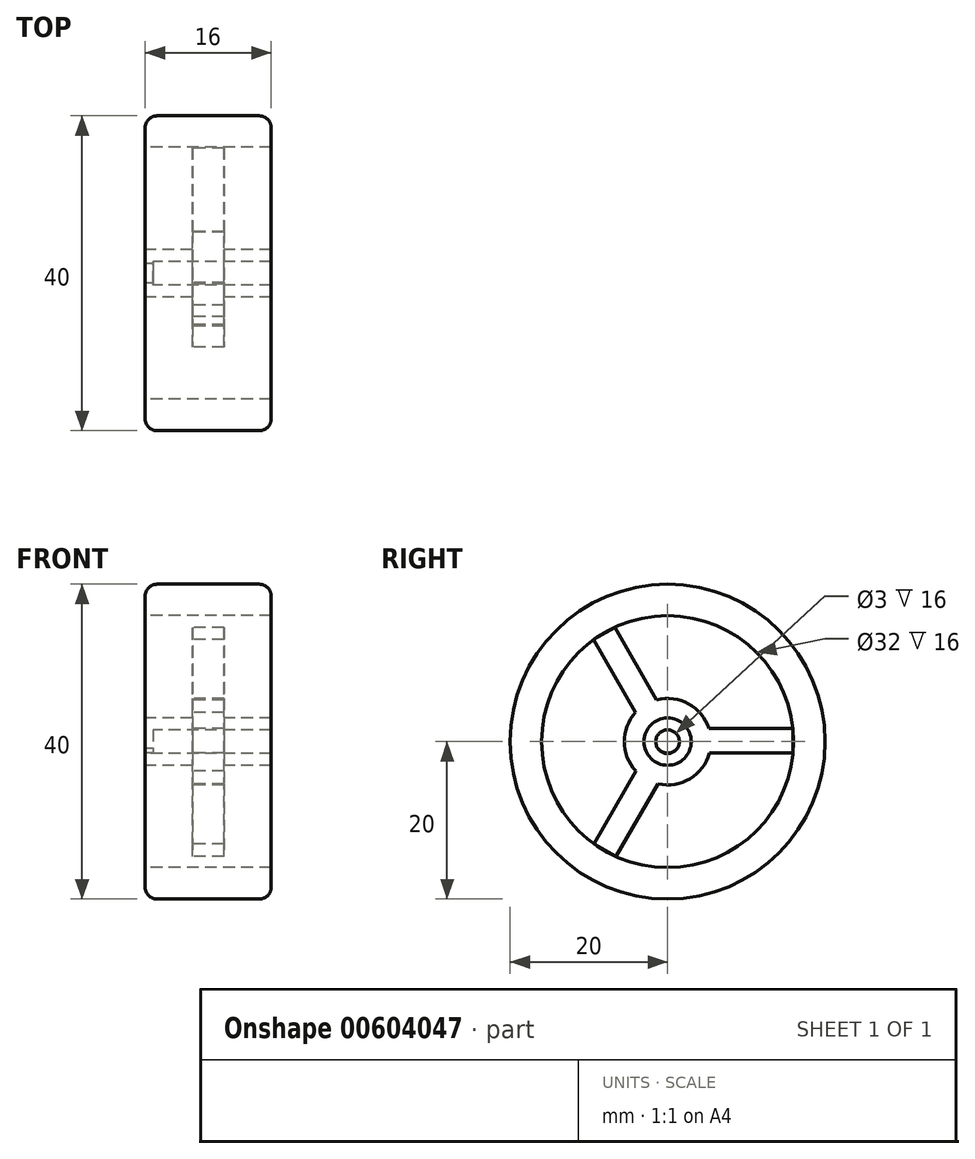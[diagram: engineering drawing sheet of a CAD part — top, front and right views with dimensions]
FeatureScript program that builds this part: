
annotation { "Feature Type Name" : "Feature", "Feature Type Description" : "" }
export const myFeature = defineFeature(function(context is Context, id is Id, definition is map)
    precondition{}
    {
        {
            var Q0;
            Q0=qCreatedBy(makeId("Front.planeOp"),FACE);
            var sketch = newSketch(context, id + "F0", { "sketchPlane" : qUnion([Q0])});
            skLineSegment(sketch, "E0.bottom", {"start": v(0, 0) * mm, "end": v(16, 0) * mm});
            skLineSegment(sketch, "E1.bottom", {"start": v(6, 0) * mm, "end": v(10, 0) * mm});
            skLineSegment(sketch, "E1.top", {"start": v(6, -16) * mm, "end": v(10, -16) * mm});
            skLineSegment(sketch, "E1.left", {"start": v(6, -13) * mm, "end": v(6, -14.5) * mm});
            skLineSegment(sketch, "E1.right", {"start": v(10, -13) * mm, "end": v(10, -14.5) * mm});
            skLineSegment(sketch, "E2.bottom", {"start": v(0, -16) * mm, "end": v(16, -16) * mm, "construction": true});
            skLineSegment(sketch, "E2.top", {"start": v(0, -13) * mm, "end": v(16, -13) * mm});
            skLineSegment(sketch, "E2.left", {"start": v(0, -14.5) * mm, "end": v(0, -13) * mm});
            skLineSegment(sketch, "E3", {"start": v(16, -14.5) * mm, "end": v(0, -14.5) * mm});
            skLineSegment(sketch, "E4", {"start": v(16, -14.5) * mm, "end": v(16, -13) * mm});
            skLineSegment(sketch, "E5.bottom", {"start": v(10, -13) * mm, "end": v(6, -13) * mm});
            skLineSegment(sketch, "E5.top", {"start": v(10, -10.5) * mm, "end": v(6, -10.5) * mm});
            skLineSegment(sketch, "E5.left", {"start": v(10, -13) * mm, "end": v(10, -10.5) * mm});
            skLineSegment(sketch, "E5.right", {"start": v(6, -13) * mm, "end": v(6, -10.5) * mm});
            skArc(sketch, "E6", {"start": v(1.5, 4) * mm, "mid": v(0.44, 3.56) * mm, "end": v(0, 2.5) * mm});
            skLineSegment(sketch, "E7", {"start": v(16, 4.74) * mm, "end": v(14.5, 4.74) * mm});
            skArc(sketch, "E8", {"start": v(16, 2.5) * mm, "mid": v(15.56, 3.56) * mm, "end": v(14.5, 4) * mm});
            skLineSegment(sketch, "E9", {"start": v(0, 2.5) * mm, "end": v(0, 0) * mm});
            skLineSegment(sketch, "E10", {"start": v(16, 0) * mm, "end": v(16, 2.5) * mm});
            skLineSegment(sketch, "E11", {"start": v(14.5, 4) * mm, "end": v(1.5, 4) * mm});
            skPoint(sketch, "E12.end.orphan", {"position": v(8, 0) * mm});
            skPoint(sketch, "E12.start.orphan", {"position": v(8, -10.5) * mm});
            skSolve(sketch);
        }
        {
            var Q0;
            Q0=qSketchRegion(id+"F0",true);
            var Q1;
            Q1=sQuery(id+"F0.wireOp",EDGE,"E1.top");
            revolve(context, id + "F1", {"entities" : qUnion([Q0]), "axis" : qUnion([Q1]), "revolveType" : RevolveType.FULL});
        }
        {
            var Q0;
            Q0=makeQuery(id+"F1.opRevolve","SWEPT_FACE",FACE,{"disambiguationData":[OSD([sQuery(id+"F0.wireOp",EDGE,"E5.right"),sQuery(id+"F0.wireOp",EDGE,"ZnnQBpbw-xC8R-MT8B-JQXv-VcrKk8POS6gG")])]});
            var sketch = newSketch(context, id + "F2", { "sketchPlane" : qUnion([Q0])});
            skLineSegment(sketch, "E13", {"start": v(-2.5, -14.35) * mm, "end": v(-15.91, -14.35) * mm});
            skLineSegment(sketch, "E14.1.1", {"start": v(-0.18, -19) * mm, "end": v(6.53, -30.6) * mm});
            skLineSegment(sketch, "E14.2.1", {"start": v(2.68, -14.65) * mm, "end": v(9.39, -3.04) * mm});
            skPoint(sketch, "E14.center", {"position": v(0, -16) * mm});
            skLineSegment(sketch, "E15", {"start": v(-15.91, -14.35) * mm, "end": v(-15.91, -17.46) * mm});
            skLineSegment(sketch, "E16", {"start": v(-15.91, -17.46) * mm, "end": v(-2.62, -17.46) * mm});
            skLineSegment(sketch, "E17", {"start": v(9.39, -3.04) * mm, "end": v(6.7, -1.49) * mm});
            skLineSegment(sketch, "E18", {"start": v(6.53, -30.6) * mm, "end": v(9.37, -28.97) * mm});
            skPoint(sketch, "E18.endSnap0", {"position": v(9.37, -29.3) * mm});
            skLineSegment(sketch, "E19", {"start": v(9.37, -28.97) * mm, "end": v(2.73, -17.46) * mm});
            skLineSegment(sketch, "E20", {"start": v(6.7, -1.49) * mm, "end": v(0.04, -13) * mm});
            skSolve(sketch);
        }
        {
            var Q0;
            {var subQ0=sQuery(id+"F2.wireOp",EDGE,"E17");Q0=makeQuery(id+"F2.imprint","IMPRINT",FACE,{"disambiguationData":[TD([[makeQuery(id+"F2.imprint","IMPRINT",EDGE,{"derivedFrom":subQ0}),1.0]])]});}
            var Q1;
            {var subQ0=sQuery(id+"F2.wireOp",EDGE,"E18");Q1=makeQuery(id+"F2.imprint","IMPRINT",FACE,{"disambiguationData":[TD([[makeQuery(id+"F2.imprint","IMPRINT",EDGE,{"derivedFrom":subQ0}),1.0]])]});}
            var Q2;
            {var subQ0=sQuery(id+"F2.wireOp",EDGE,"E15");Q2=makeQuery(id+"F2.imprint","IMPRINT",FACE,{"disambiguationData":[TD([[makeQuery(id+"F2.imprint","IMPRINT",EDGE,{"derivedFrom":subQ0}),1.0]])]});}
            extrude(context, id + "F3", {"entities" : qUnion([Q0, Q1, Q2]), "operationType" : NewBodyOperationType.ADD, "oppositeDirection" : true, "depth" : 4 * mm});
        }
        {
            var Q0;
            Q0=qCreatedBy(makeId("Right.planeOp"),FACE);
            var sketch = newSketch(context, id + "F4", { "sketchPlane" : qUnion([Q0])});
            skCircle(sketch, "E21", {"center": v(0, -15.89) * mm, "radius": 1.57 * mm});
            skSolve(sketch);
        }
        {
            var Q0;
            Q0=makeQuery(id+"F4.imprint","IMPRINT",FACE,{"disambiguationData":[TD([[makeQuery(id+"F4.imprint","IMPRINT",EDGE,{"derivedFrom":sQuery(id+"F4.wireOp",EDGE,"E21")}),1.0]])]});
            var Q1;
            Q1=sQuery(id+"F4.wireOp",EDGE,"E21");
            extrude(context, id + "F5", {"entities" : qUnion([Q0]), "operationType" : NewBodyOperationType.ADD, "surfaceEntities" : qUnion([Q1]), "depth" : 1 * mm});
        }
    });
